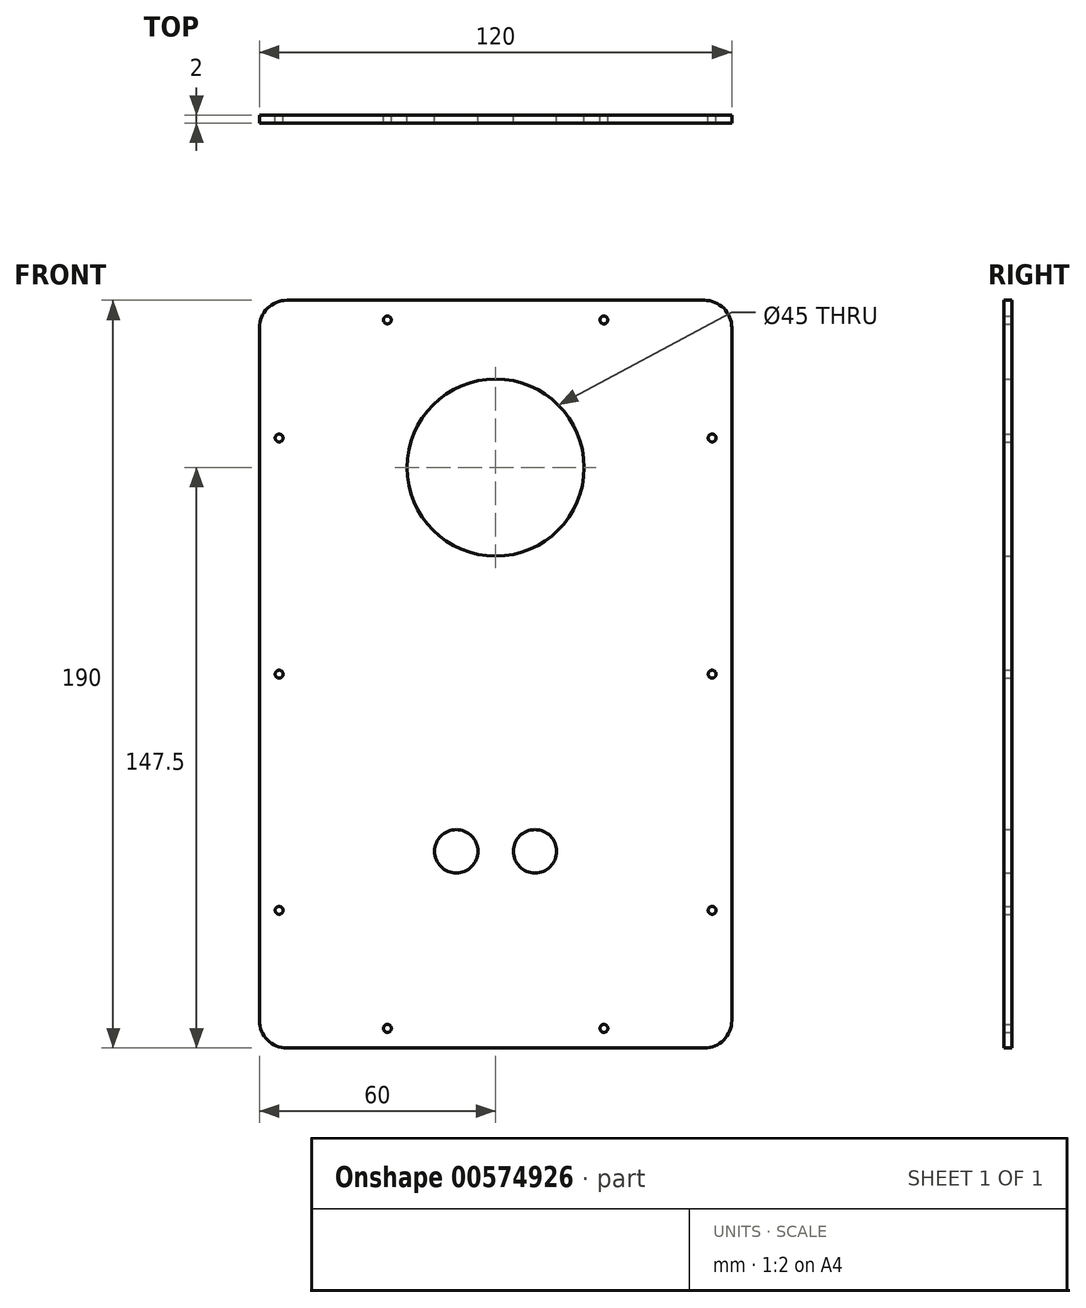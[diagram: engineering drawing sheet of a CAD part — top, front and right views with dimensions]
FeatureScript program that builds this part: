
annotation { "Feature Type Name" : "Feature", "Feature Type Description" : "" }
export const myFeature = defineFeature(function(context is Context, id is Id, definition is map)
    precondition{}
    {
        {
            var Q0;
            Q0=qCreatedBy(makeId("Front.planeOp"),FACE);
            var sketch = newSketch(context, id + "F0", { "sketchPlane" : qUnion([Q0])});
            skLineSegment(sketch, "E0.bottom", {"start": v(53, 95) * mm, "end": v(-53, 95) * mm});
            skLineSegment(sketch, "E0.top", {"start": v(53, -95) * mm, "end": v(-53, -95) * mm});
            skLineSegment(sketch, "E0.left", {"start": v(60, 88) * mm, "end": v(60, -88) * mm});
            skLineSegment(sketch, "E0.right", {"start": v(-60, 88) * mm, "end": v(-60, -88) * mm});
            skPoint(sketch, "E0.middle", {"position": v(0, 0) * mm});
            skPoint(sketch, "E1.visualSharp", {"position": v(-60, 95) * mm});
            skArc(sketch, "E1.filletArc", {"start": v(-53, 95) * mm, "mid": v(-57.95, 92.95) * mm, "end": v(-60, 88) * mm});
            skPoint(sketch, "E2.visualSharp", {"position": v(60, 95) * mm});
            skArc(sketch, "E2.filletArc", {"start": v(60, 88) * mm, "mid": v(57.95, 92.95) * mm, "end": v(53, 95) * mm});
            skPoint(sketch, "E3.visualSharp", {"position": v(60, -95) * mm});
            skArc(sketch, "E3.filletArc", {"start": v(53, -95) * mm, "mid": v(57.95, -92.95) * mm, "end": v(60, -88) * mm});
            skPoint(sketch, "E4.visualSharp", {"position": v(-60, -95) * mm});
            skArc(sketch, "E4.filletArc", {"start": v(-60, -88) * mm, "mid": v(-57.95, -92.95) * mm, "end": v(-53, -95) * mm});
            skPoint(sketch, "E5", {"position": v(-27.5, 90) * mm});
            skPoint(sketch, "E6", {"position": v(27.5, 90) * mm});
            skPoint(sketch, "E7", {"position": v(-55, -60) * mm});
            skPoint(sketch, "E8", {"position": v(-55, 60) * mm});
            skPoint(sketch, "E9", {"position": v(-55, 0) * mm});
            skPoint(sketch, "E10.MirrorP", {"position": v(55, 60) * mm});
            skPoint(sketch, "E11.MirrorP", {"position": v(55, 0) * mm});
            skPoint(sketch, "E12.MirrorP", {"position": v(55, -60) * mm});
            skPoint(sketch, "E13.MirrorP", {"position": v(-27.5, -90) * mm});
            skPoint(sketch, "E14.MirrorP", {"position": v(27.5, -90) * mm});
            skCircle(sketch, "E15", {"center": v(-10, -45) * mm, "radius": 5.5 * mm});
            skCircle(sketch, "E16", {"center": v(10, -45) * mm, "radius": 5.5 * mm});
            skLineSegment(sketch, "E17", {"start": v(0, 0) * mm, "end": v(0, -64.73) * mm, "construction": true});
            skCircle(sketch, "E18", {"center": v(0, 52.5) * mm, "radius": 22.5 * mm});
            skSolve(sketch);
        }
        {
            var Q0;
            Q0=makeQuery(id+"F0.imprint","IMPRINT",FACE,{"disambiguationData":[TD([[makeQuery(id+"F0.imprint","IMPRINT",EDGE,{"derivedFrom":sQuery(id+"F0.wireOp",EDGE,"E0.bottom")}),1.0]])]});
            extrude(context, id + "F1", {"entities" : qUnion([Q0]), "depth" : 2 * mm, "offsetDistance" : 25 * mm});
        }
        {
            var Q0;
            Q0=sQuery(id+"F0.wireOp",VERTEX,"E5");
            var Q1;
            Q1=sQuery(id+"F0.wireOp",VERTEX,"E8");
            var Q2;
            Q2=sQuery(id+"F0.wireOp",VERTEX,"E9");
            var Q3;
            Q3=sQuery(id+"F0.wireOp",VERTEX,"E7");
            var Q4;
            Q4=sQuery(id+"F0.wireOp",VERTEX,"E13.MirrorP");
            var Q5;
            Q5=sQuery(id+"F0.wireOp",VERTEX,"E14.MirrorP");
            var Q6;
            Q6=sQuery(id+"F0.wireOp",VERTEX,"E12.MirrorP");
            var Q7;
            Q7=sQuery(id+"F0.wireOp",VERTEX,"E11.MirrorP");
            var Q8;
            Q8=sQuery(id+"F0.wireOp",VERTEX,"E10.MirrorP");
            var Q9;
            Q9=sQuery(id+"F0.wireOp",VERTEX,"E6");
            var Q10;
            Q10=makeQuery(id+"F1.opExtrude","SWEPT_BODY",BODY,{"disambiguationData":[OSD([sQuery(id+"F0.wireOp",EDGE,"E0.bottom"),sQuery(id+"F0.wireOp",EDGE,"E0.top"),sQuery(id+"F0.wireOp",EDGE,"E0.left"),sQuery(id+"F0.wireOp",EDGE,"E0.right"),sQuery(id+"F0.wireOp",EDGE,"E1.filletArc"),sQuery(id+"F0.wireOp",EDGE,"E2.filletArc"),sQuery(id+"F0.wireOp",EDGE,"E3.filletArc"),sQuery(id+"F0.wireOp",EDGE,"E4.filletArc")])]});
            hole(context, id + "F2", {"style" : HoleStyle.SIMPLE, "endStyle" : HoleEndStyle.THROUGH, "oppositeDirection" : true, "holeDiameter" : 2 * mm, "isTappedThrough" : true, "tappedDepth" : 12 * mm, "tapClearance" : 3, "locations" : qUnion([Q0, Q1, Q2, Q3, Q4, Q5, Q6, Q7, Q8, Q9]), "scope" : qUnion([Q10])});
        }
    });
